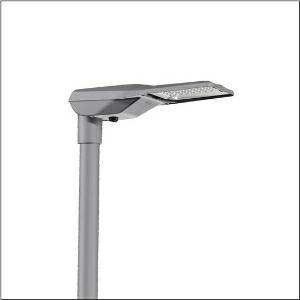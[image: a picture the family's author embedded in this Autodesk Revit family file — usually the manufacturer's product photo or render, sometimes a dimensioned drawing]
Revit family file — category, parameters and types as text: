
# Revit family: streetlight_sl_21_iq_mini___st1_0ab_5xe2m31u08jb_1fa0
name_source: partatom
category: Lighting Fixtures
units: mm (PartAtom-declared; Revit-internal decimal feet)

## family parameters
Cut with Voids When Loaded = No
Host = Face
Light Source = No
Part Type = Normal
Room Calculation Point = No
Round Connector Dimension = Use Diameter
Shared = No

## types (1)
- --- (1 x LED, 9870 lm, 72.5 W, 3000K)
    Apparent Load = 73 VA
    CIE Flux Codes = 40 74 97 100 100
    Color Rendering = 70
    Color Temperature = 3000K
    Default Elevation = 1800 mm
    Description = Streetlight SL 21 iQ mini, mast luminaire, primary light control with lens, of PMMA, primary optical cover: cover, of toughened safety glass, transparent, light distribution: ST1.0aB, light emission: direct distribution, primary light characteristic: asymmetric, installation type: post-top, side-entry, LED, High Power LED, rated luminous flux: 9.870lm, luminous efficacy: 136lm/W, light colour: 730, colour temperature: 3000K, control gear: iQ-Street Remote, D4i with power reduction, control: pre-setting: logarithmic dimming characteristic, Street-Remote, Auto-Match, Temp-Guard, Lumen-Switch, Night-Set, Smart-Wire, Light-Fading, Desk-Remote (wireless, voltage-free reading and setting of iQ features in the workshop via application-optimized NFC function/RFID function), optimised constant luminous flux control (CLO 2.0), mains connection: 220..240V, AC, 50/60Hz, start of lifetime: 73W, end of service life: 76W, reduction: 33W, luminaire housing, of diecast aluminium, powder-coated, Siteco® metallic grey (DB 702S), corrosivity category C5 mid according to DIN EN ISO 12944, please order mast flange separately, inclination adjustable: 0°, 5°, 10°, 15°, sealing non-destructively replaceable, multi-level sealing system, length: 628mm, width: 235mm, height: 110mm, mast flange for spigot size: 42mm (side-entry): 5XC10008XM4, 60/48mm (side-entry/post-top): 5XC10108XM2, 76/60mm (side-entry/post-top): 5XC10108XM1, mounting height: 4..8m, Smart Interface below, protection rating (complete): IP66, insulation class (complete): insulation class II (safety insulation), certification: CE, ENEC, ENEC+, VDE, impact resistance: IK10, permissible operating ambient temperature for outdoor applications: -40..+50°C, standard-compliant lighting for roads and squares, packaging unit: 1 piece

Light Distribution: ST1.0aB
    Height = 110 mm
    Lamp = 1 x LED
    Lamp Light Flux = 9870 lm
    Lamp Power = 72.5 W
    Lamp count = 1
    Length = 625 mm
    Luminous efficacy = 136 lm/W
    Manufacturer = Siteco
    ModVariant = No
    Model = 5XE2M31U08JB
    Number of Poles = 1
    OnlyDefault = Yes
    Power Factor = 1
    Product Name = Streetlight SL 21 iQ mini | ST1.0aB
    Product group = mast luminaire | pylon top
    ProductGroupID = 6100
    Protection Class = Protection class II
    Protection Degree = IP 66
    RLX_Detail_Level = 1
    RLX_Emergency_Light_Flux = 0 lm
    RLX_Emergency_Type = 0
    RLX_Emergency_Type_DB = No
    RlxData = <blob elided: 26593 chars, md5=14f7c561>
    Socket = socket
    Standby Power = 0 W
    System Light Flux = 9870 lm
    System Power = 73 W
    Type Comments = factory setting: luminous flux: 100 % | dim-lin: 254 | 755 mA
    Type Image = l_1003516.jpg
    URL = http://relux.com
    VarID = @adj_112248
    Voltage = 0 V
    Weight = 0.00 kg
    Width = 234 mm

## geometry (parser evidence)
native form markers: Blend x4, Sweep x12
no freeform markers — native parametric forms only
